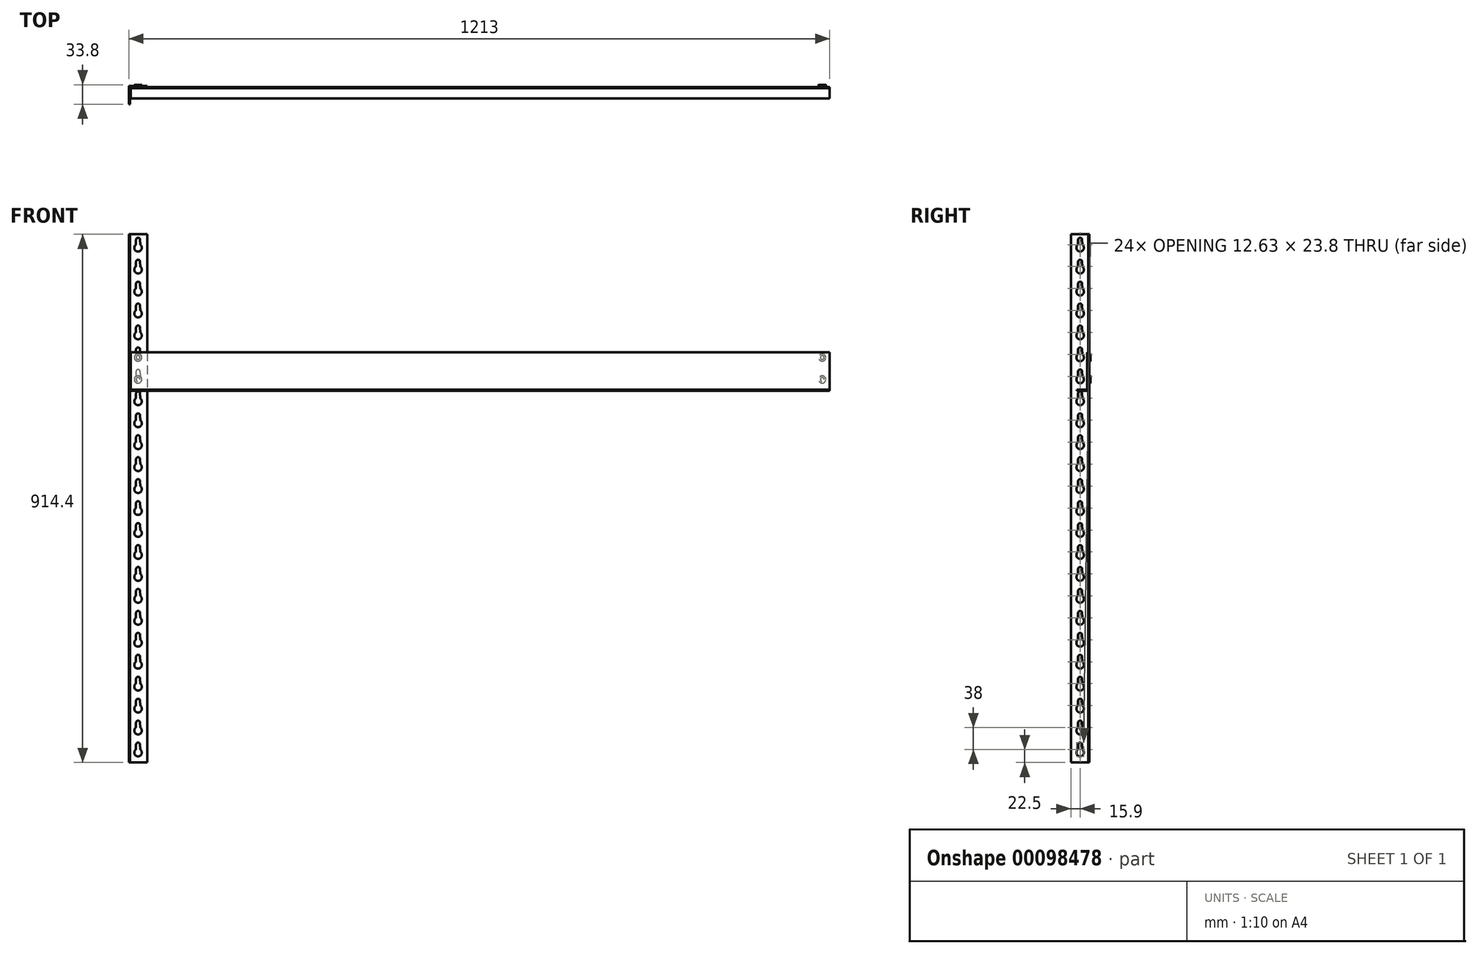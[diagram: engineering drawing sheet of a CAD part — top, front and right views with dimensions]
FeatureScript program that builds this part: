
annotation { "Feature Type Name" : "Feature", "Feature Type Description" : "" }
export const myFeature = defineFeature(function(context is Context, id is Id, definition is map)
    precondition{}
    {
        {
            var Q0;
            Q0=qCreatedBy(makeId("Top.planeOp"),FACE);
            var sketch = newSketch(context, id + "F0", { "sketchPlane" : qUnion([Q0])});
            skLineSegment(sketch, "E0.bottom", {"start": v(-13.9, -15.9) * mm, "end": v(-15.9, -15.9) * mm});
            skLineSegment(sketch, "E0.top", {"start": v(15.9, 15.9) * mm, "end": v(-14.9, 15.9) * mm});
            skLineSegment(sketch, "E0.left", {"start": v(15.9, 13.9) * mm, "end": v(15.9, 15.9) * mm});
            skLineSegment(sketch, "E0.right", {"start": v(-15.9, -15.9) * mm, "end": v(-15.9, 14.9) * mm});
            skPoint(sketch, "E0.middle", {"position": v(0, 0) * mm});
            skLineSegment(sketch, "E1.0", {"start": v(13.9, 13.9) * mm, "end": v(-12.9, 13.9) * mm});
            skLineSegment(sketch, "E1.3", {"start": v(-13.9, -13.9) * mm, "end": v(-13.9, 12.9) * mm});
            skLineSegment(sketch, "E2", {"start": v(13.9, 13.9) * mm, "end": v(15.9, 13.9) * mm});
            skLineSegment(sketch, "E3", {"start": v(-13.9, -13.9) * mm, "end": v(-13.9, -15.9) * mm});
            skPoint(sketch, "E4.orphan", {"position": v(15.9, -15.9) * mm});
            skPoint(sketch, "E5.visualSharp", {"position": v(-15.9, 15.9) * mm});
            skArc(sketch, "E5.filletArc", {"start": v(-14.9, 15.9) * mm, "mid": v(-15.6, 15.6) * mm, "end": v(-15.9, 14.9) * mm});
            skPoint(sketch, "E6.visualSharp", {"position": v(-13.9, 13.9) * mm});
            skArc(sketch, "E6.filletArc", {"start": v(-12.9, 13.9) * mm, "mid": v(-13.6, 13.6) * mm, "end": v(-13.9, 12.9) * mm});
            skSolve(sketch);
        }
        {
            var Q0;
            Q0 = qSketchRegion(id + "F0", true);
            extrude(context, id + "F1", {"entities" : qUnion([Q0]), "depth" : 914.4 * mm});
        }
        {
            var Q0;
            Q0=makeQuery(id+"F1.opExtrude","SWEPT_FACE",FACE,{"disambiguationData":[OSD([sQuery(id+"F0.wireOp",EDGE,"E0.right")])]});
            var sketch = newSketch(context, id + "F2", { "sketchPlane" : qUnion([Q0])});
            skArc(sketch, "E7", {"start": v(-4.32, 895.96) * mm, "mid": v(0, 884.6) * mm, "end": v(4.32, 895.96) * mm});
            skArc(sketch, "E8", {"start": v(3.5, 904.9) * mm, "mid": v(0, 908.4) * mm, "end": v(-3.5, 904.9) * mm});
            skLineSegment(sketch, "E9", {"start": v(0, 904.9) * mm, "end": v(-3.5, 904.9) * mm, "construction": true});
            skLineSegment(sketch, "E10", {"start": v(0, 891.1) * mm, "end": v(-6.5, 891.1) * mm, "construction": true});
            skLineSegment(sketch, "E11", {"start": v(0, 904.9) * mm, "end": v(0, 891.1) * mm, "construction": true});
            skLineSegment(sketch, "E12", {"start": v(-3.5, 904.9) * mm, "end": v(-3.65, 897.41) * mm});
            skLineSegment(sketch, "E13.MirrorCS", {"start": v(3.5, 904.9) * mm, "end": v(3.65, 897.41) * mm});
            skPoint(sketch, "E14.visualSharp", {"position": v(-3.67, 896.47) * mm});
            skArc(sketch, "E14.filletArc", {"start": v(-4.32, 895.96) * mm, "mid": v(-3.83, 896.61) * mm, "end": v(-3.65, 897.41) * mm});
            skPoint(sketch, "E15.visualSharp", {"position": v(3.67, 896.47) * mm});
            skArc(sketch, "E15.filletArc", {"start": v(3.65, 897.41) * mm, "mid": v(3.83, 896.61) * mm, "end": v(4.32, 895.96) * mm});
            skArc(sketch, "E16.0.1.0", {"start": v(3.5, 866.9) * mm, "mid": v(0, 870.4) * mm, "end": v(-3.5, 866.9) * mm});
            skLineSegment(sketch, "E16.0.1.1", {"start": v(-3.5, 866.9) * mm, "end": v(-3.65, 859.41) * mm});
            skLineSegment(sketch, "E16.0.1.2", {"start": v(3.5, 866.9) * mm, "end": v(3.65, 859.41) * mm});
            skArc(sketch, "E16.0.1.3", {"start": v(-4.32, 857.96) * mm, "mid": v(0, 846.6) * mm, "end": v(4.32, 857.96) * mm});
            skArc(sketch, "E16.0.1.4", {"start": v(-4.32, 857.96) * mm, "mid": v(-3.83, 858.61) * mm, "end": v(-3.65, 859.41) * mm});
            skArc(sketch, "E16.0.1.5", {"start": v(3.65, 859.41) * mm, "mid": v(3.83, 858.61) * mm, "end": v(4.32, 857.96) * mm});
            skArc(sketch, "E16.0.2.0", {"start": v(3.5, 828.9) * mm, "mid": v(0, 832.4) * mm, "end": v(-3.5, 828.9) * mm});
            skLineSegment(sketch, "E16.0.2.1", {"start": v(-3.5, 828.9) * mm, "end": v(-3.65, 821.41) * mm});
            skLineSegment(sketch, "E16.0.2.2", {"start": v(3.5, 828.9) * mm, "end": v(3.65, 821.41) * mm});
            skArc(sketch, "E16.0.2.3", {"start": v(-4.32, 819.96) * mm, "mid": v(0, 808.6) * mm, "end": v(4.32, 819.96) * mm});
            skArc(sketch, "E16.0.2.4", {"start": v(-4.32, 819.96) * mm, "mid": v(-3.83, 820.61) * mm, "end": v(-3.65, 821.41) * mm});
            skArc(sketch, "E16.0.2.5", {"start": v(3.65, 821.41) * mm, "mid": v(3.83, 820.61) * mm, "end": v(4.32, 819.96) * mm});
            skArc(sketch, "E16.0.3.0", {"start": v(3.5, 790.9) * mm, "mid": v(0, 794.4) * mm, "end": v(-3.5, 790.9) * mm});
            skLineSegment(sketch, "E16.0.3.1", {"start": v(-3.5, 790.9) * mm, "end": v(-3.65, 783.41) * mm});
            skLineSegment(sketch, "E16.0.3.2", {"start": v(3.5, 790.9) * mm, "end": v(3.65, 783.41) * mm});
            skArc(sketch, "E16.0.3.3", {"start": v(-4.32, 781.96) * mm, "mid": v(0, 770.6) * mm, "end": v(4.32, 781.96) * mm});
            skArc(sketch, "E16.0.3.4", {"start": v(-4.32, 781.96) * mm, "mid": v(-3.83, 782.61) * mm, "end": v(-3.65, 783.41) * mm});
            skArc(sketch, "E16.0.3.5", {"start": v(3.65, 783.41) * mm, "mid": v(3.83, 782.61) * mm, "end": v(4.32, 781.96) * mm});
            skArc(sketch, "E16.0.4.0", {"start": v(3.5, 752.9) * mm, "mid": v(0, 756.4) * mm, "end": v(-3.5, 752.9) * mm});
            skLineSegment(sketch, "E16.0.4.1", {"start": v(-3.5, 752.9) * mm, "end": v(-3.65, 745.41) * mm});
            skLineSegment(sketch, "E16.0.4.2", {"start": v(3.5, 752.9) * mm, "end": v(3.65, 745.41) * mm});
            skArc(sketch, "E16.0.4.3", {"start": v(-4.32, 743.96) * mm, "mid": v(0, 732.6) * mm, "end": v(4.32, 743.96) * mm});
            skArc(sketch, "E16.0.4.4", {"start": v(-4.32, 743.96) * mm, "mid": v(-3.83, 744.61) * mm, "end": v(-3.65, 745.41) * mm});
            skArc(sketch, "E16.0.4.5", {"start": v(3.65, 745.41) * mm, "mid": v(3.83, 744.61) * mm, "end": v(4.32, 743.96) * mm});
            skArc(sketch, "E16.0.5.0", {"start": v(3.5, 714.9) * mm, "mid": v(0, 718.4) * mm, "end": v(-3.5, 714.9) * mm});
            skLineSegment(sketch, "E16.0.5.1", {"start": v(-3.5, 714.9) * mm, "end": v(-3.65, 707.41) * mm});
            skLineSegment(sketch, "E16.0.5.2", {"start": v(3.5, 714.9) * mm, "end": v(3.65, 707.41) * mm});
            skArc(sketch, "E16.0.5.3", {"start": v(-4.32, 705.96) * mm, "mid": v(0, 694.6) * mm, "end": v(4.32, 705.96) * mm});
            skArc(sketch, "E16.0.5.4", {"start": v(-4.32, 705.96) * mm, "mid": v(-3.83, 706.61) * mm, "end": v(-3.65, 707.41) * mm});
            skArc(sketch, "E16.0.5.5", {"start": v(3.65, 707.41) * mm, "mid": v(3.83, 706.61) * mm, "end": v(4.32, 705.96) * mm});
            skArc(sketch, "E16.0.6.0", {"start": v(3.5, 676.9) * mm, "mid": v(0, 680.4) * mm, "end": v(-3.5, 676.9) * mm});
            skLineSegment(sketch, "E16.0.6.1", {"start": v(-3.5, 676.9) * mm, "end": v(-3.65, 669.41) * mm});
            skLineSegment(sketch, "E16.0.6.2", {"start": v(3.5, 676.9) * mm, "end": v(3.65, 669.41) * mm});
            skArc(sketch, "E16.0.6.3", {"start": v(-4.32, 667.96) * mm, "mid": v(0, 656.6) * mm, "end": v(4.32, 667.96) * mm});
            skArc(sketch, "E16.0.6.4", {"start": v(-4.32, 667.96) * mm, "mid": v(-3.83, 668.61) * mm, "end": v(-3.65, 669.41) * mm});
            skArc(sketch, "E16.0.6.5", {"start": v(3.65, 669.41) * mm, "mid": v(3.83, 668.61) * mm, "end": v(4.32, 667.96) * mm});
            skArc(sketch, "E16.0.7.0", {"start": v(3.5, 638.9) * mm, "mid": v(0, 642.4) * mm, "end": v(-3.5, 638.9) * mm});
            skLineSegment(sketch, "E16.0.7.1", {"start": v(-3.5, 638.9) * mm, "end": v(-3.65, 631.41) * mm});
            skLineSegment(sketch, "E16.0.7.2", {"start": v(3.5, 638.9) * mm, "end": v(3.65, 631.41) * mm});
            skArc(sketch, "E16.0.7.3", {"start": v(-4.32, 629.96) * mm, "mid": v(0, 618.6) * mm, "end": v(4.32, 629.96) * mm});
            skArc(sketch, "E16.0.7.4", {"start": v(-4.32, 629.96) * mm, "mid": v(-3.83, 630.61) * mm, "end": v(-3.65, 631.41) * mm});
            skArc(sketch, "E16.0.7.5", {"start": v(3.65, 631.41) * mm, "mid": v(3.83, 630.61) * mm, "end": v(4.32, 629.96) * mm});
            skArc(sketch, "E16.0.8.0", {"start": v(3.5, 600.9) * mm, "mid": v(0, 604.4) * mm, "end": v(-3.5, 600.9) * mm});
            skLineSegment(sketch, "E16.0.8.1", {"start": v(-3.5, 600.9) * mm, "end": v(-3.65, 593.41) * mm});
            skLineSegment(sketch, "E16.0.8.2", {"start": v(3.5, 600.9) * mm, "end": v(3.65, 593.41) * mm});
            skArc(sketch, "E16.0.8.3", {"start": v(-4.32, 591.96) * mm, "mid": v(0, 580.6) * mm, "end": v(4.32, 591.96) * mm});
            skArc(sketch, "E16.0.8.4", {"start": v(-4.32, 591.96) * mm, "mid": v(-3.83, 592.61) * mm, "end": v(-3.65, 593.41) * mm});
            skArc(sketch, "E16.0.8.5", {"start": v(3.65, 593.41) * mm, "mid": v(3.83, 592.61) * mm, "end": v(4.32, 591.96) * mm});
            skArc(sketch, "E16.0.9.0", {"start": v(3.5, 562.9) * mm, "mid": v(0, 566.4) * mm, "end": v(-3.5, 562.9) * mm});
            skLineSegment(sketch, "E16.0.9.1", {"start": v(-3.5, 562.9) * mm, "end": v(-3.65, 555.41) * mm});
            skLineSegment(sketch, "E16.0.9.2", {"start": v(3.5, 562.9) * mm, "end": v(3.65, 555.41) * mm});
            skArc(sketch, "E16.0.9.3", {"start": v(-4.32, 553.96) * mm, "mid": v(0, 542.6) * mm, "end": v(4.32, 553.96) * mm});
            skArc(sketch, "E16.0.9.4", {"start": v(-4.32, 553.96) * mm, "mid": v(-3.83, 554.61) * mm, "end": v(-3.65, 555.41) * mm});
            skArc(sketch, "E16.0.9.5", {"start": v(3.65, 555.41) * mm, "mid": v(3.83, 554.61) * mm, "end": v(4.32, 553.96) * mm});
            skArc(sketch, "E16.0.10.0", {"start": v(3.5, 524.9) * mm, "mid": v(0, 528.4) * mm, "end": v(-3.5, 524.9) * mm});
            skLineSegment(sketch, "E16.0.10.1", {"start": v(-3.5, 524.9) * mm, "end": v(-3.65, 517.41) * mm});
            skLineSegment(sketch, "E16.0.10.2", {"start": v(3.5, 524.9) * mm, "end": v(3.65, 517.41) * mm});
            skArc(sketch, "E16.0.10.3", {"start": v(-4.32, 515.96) * mm, "mid": v(0, 504.6) * mm, "end": v(4.32, 515.96) * mm});
            skArc(sketch, "E16.0.10.4", {"start": v(-4.32, 515.96) * mm, "mid": v(-3.83, 516.61) * mm, "end": v(-3.65, 517.41) * mm});
            skArc(sketch, "E16.0.10.5", {"start": v(3.65, 517.41) * mm, "mid": v(3.83, 516.61) * mm, "end": v(4.32, 515.96) * mm});
            skArc(sketch, "E16.0.11.0", {"start": v(3.5, 486.9) * mm, "mid": v(0, 490.4) * mm, "end": v(-3.5, 486.9) * mm});
            skLineSegment(sketch, "E16.0.11.1", {"start": v(-3.5, 486.9) * mm, "end": v(-3.65, 479.41) * mm});
            skLineSegment(sketch, "E16.0.11.2", {"start": v(3.5, 486.9) * mm, "end": v(3.65, 479.41) * mm});
            skArc(sketch, "E16.0.11.3", {"start": v(-4.32, 477.96) * mm, "mid": v(0, 466.6) * mm, "end": v(4.32, 477.96) * mm});
            skArc(sketch, "E16.0.11.4", {"start": v(-4.32, 477.96) * mm, "mid": v(-3.83, 478.61) * mm, "end": v(-3.65, 479.41) * mm});
            skArc(sketch, "E16.0.11.5", {"start": v(3.65, 479.41) * mm, "mid": v(3.83, 478.61) * mm, "end": v(4.32, 477.96) * mm});
            skArc(sketch, "E16.0.12.0", {"start": v(3.5, 448.9) * mm, "mid": v(0, 452.4) * mm, "end": v(-3.5, 448.9) * mm});
            skLineSegment(sketch, "E16.0.12.1", {"start": v(-3.5, 448.9) * mm, "end": v(-3.65, 441.41) * mm});
            skLineSegment(sketch, "E16.0.12.2", {"start": v(3.5, 448.9) * mm, "end": v(3.65, 441.41) * mm});
            skArc(sketch, "E16.0.12.3", {"start": v(-4.32, 439.96) * mm, "mid": v(0, 428.6) * mm, "end": v(4.32, 439.96) * mm});
            skArc(sketch, "E16.0.12.4", {"start": v(-4.32, 439.96) * mm, "mid": v(-3.83, 440.61) * mm, "end": v(-3.65, 441.41) * mm});
            skArc(sketch, "E16.0.12.5", {"start": v(3.65, 441.41) * mm, "mid": v(3.83, 440.61) * mm, "end": v(4.32, 439.96) * mm});
            skArc(sketch, "E16.0.13.0", {"start": v(3.5, 410.9) * mm, "mid": v(0, 414.4) * mm, "end": v(-3.5, 410.9) * mm});
            skLineSegment(sketch, "E16.0.13.1", {"start": v(-3.5, 410.9) * mm, "end": v(-3.65, 403.41) * mm});
            skLineSegment(sketch, "E16.0.13.2", {"start": v(3.5, 410.9) * mm, "end": v(3.65, 403.41) * mm});
            skArc(sketch, "E16.0.13.3", {"start": v(-4.32, 401.96) * mm, "mid": v(0, 390.6) * mm, "end": v(4.32, 401.96) * mm});
            skArc(sketch, "E16.0.13.4", {"start": v(-4.32, 401.96) * mm, "mid": v(-3.83, 402.61) * mm, "end": v(-3.65, 403.41) * mm});
            skArc(sketch, "E16.0.13.5", {"start": v(3.65, 403.41) * mm, "mid": v(3.83, 402.61) * mm, "end": v(4.32, 401.96) * mm});
            skArc(sketch, "E16.0.14.0", {"start": v(3.5, 372.9) * mm, "mid": v(0, 376.4) * mm, "end": v(-3.5, 372.9) * mm});
            skLineSegment(sketch, "E16.0.14.1", {"start": v(-3.5, 372.9) * mm, "end": v(-3.65, 365.41) * mm});
            skLineSegment(sketch, "E16.0.14.2", {"start": v(3.5, 372.9) * mm, "end": v(3.65, 365.41) * mm});
            skArc(sketch, "E16.0.14.3", {"start": v(-4.32, 363.96) * mm, "mid": v(0, 352.6) * mm, "end": v(4.32, 363.96) * mm});
            skArc(sketch, "E16.0.14.4", {"start": v(-4.32, 363.96) * mm, "mid": v(-3.83, 364.61) * mm, "end": v(-3.65, 365.41) * mm});
            skArc(sketch, "E16.0.14.5", {"start": v(3.65, 365.41) * mm, "mid": v(3.83, 364.61) * mm, "end": v(4.32, 363.96) * mm});
            skArc(sketch, "E16.0.15.0", {"start": v(3.5, 334.9) * mm, "mid": v(0, 338.4) * mm, "end": v(-3.5, 334.9) * mm});
            skLineSegment(sketch, "E16.0.15.1", {"start": v(-3.5, 334.9) * mm, "end": v(-3.65, 327.41) * mm});
            skLineSegment(sketch, "E16.0.15.2", {"start": v(3.5, 334.9) * mm, "end": v(3.65, 327.41) * mm});
            skArc(sketch, "E16.0.15.3", {"start": v(-4.32, 325.96) * mm, "mid": v(0, 314.6) * mm, "end": v(4.32, 325.96) * mm});
            skArc(sketch, "E16.0.15.4", {"start": v(-4.32, 325.96) * mm, "mid": v(-3.83, 326.61) * mm, "end": v(-3.65, 327.41) * mm});
            skArc(sketch, "E16.0.15.5", {"start": v(3.65, 327.41) * mm, "mid": v(3.83, 326.61) * mm, "end": v(4.32, 325.96) * mm});
            skArc(sketch, "E16.0.16.0", {"start": v(3.5, 296.9) * mm, "mid": v(0, 300.4) * mm, "end": v(-3.5, 296.9) * mm});
            skLineSegment(sketch, "E16.0.16.1", {"start": v(-3.5, 296.9) * mm, "end": v(-3.65, 289.41) * mm});
            skLineSegment(sketch, "E16.0.16.2", {"start": v(3.5, 296.9) * mm, "end": v(3.65, 289.41) * mm});
            skArc(sketch, "E16.0.16.3", {"start": v(-4.32, 287.96) * mm, "mid": v(0, 276.6) * mm, "end": v(4.32, 287.96) * mm});
            skArc(sketch, "E16.0.16.4", {"start": v(-4.32, 287.96) * mm, "mid": v(-3.83, 288.61) * mm, "end": v(-3.65, 289.41) * mm});
            skArc(sketch, "E16.0.16.5", {"start": v(3.65, 289.41) * mm, "mid": v(3.83, 288.61) * mm, "end": v(4.32, 287.96) * mm});
            skArc(sketch, "E16.0.17.0", {"start": v(3.5, 258.9) * mm, "mid": v(0, 262.4) * mm, "end": v(-3.5, 258.9) * mm});
            skLineSegment(sketch, "E16.0.17.1", {"start": v(-3.5, 258.9) * mm, "end": v(-3.65, 251.41) * mm});
            skLineSegment(sketch, "E16.0.17.2", {"start": v(3.5, 258.9) * mm, "end": v(3.65, 251.41) * mm});
            skArc(sketch, "E16.0.17.3", {"start": v(-4.32, 249.96) * mm, "mid": v(0, 238.6) * mm, "end": v(4.32, 249.96) * mm});
            skArc(sketch, "E16.0.17.4", {"start": v(-4.32, 249.96) * mm, "mid": v(-3.83, 250.61) * mm, "end": v(-3.65, 251.41) * mm});
            skArc(sketch, "E16.0.17.5", {"start": v(3.65, 251.41) * mm, "mid": v(3.83, 250.61) * mm, "end": v(4.32, 249.96) * mm});
            skArc(sketch, "E16.0.18.0", {"start": v(3.5, 220.9) * mm, "mid": v(0, 224.4) * mm, "end": v(-3.5, 220.9) * mm});
            skLineSegment(sketch, "E16.0.18.1", {"start": v(-3.5, 220.9) * mm, "end": v(-3.65, 213.41) * mm});
            skLineSegment(sketch, "E16.0.18.2", {"start": v(3.5, 220.9) * mm, "end": v(3.65, 213.41) * mm});
            skArc(sketch, "E16.0.18.3", {"start": v(-4.32, 211.96) * mm, "mid": v(0, 200.6) * mm, "end": v(4.32, 211.96) * mm});
            skArc(sketch, "E16.0.18.4", {"start": v(-4.32, 211.96) * mm, "mid": v(-3.83, 212.61) * mm, "end": v(-3.65, 213.41) * mm});
            skArc(sketch, "E16.0.18.5", {"start": v(3.65, 213.41) * mm, "mid": v(3.83, 212.61) * mm, "end": v(4.32, 211.96) * mm});
            skArc(sketch, "E16.0.19.0", {"start": v(3.5, 182.9) * mm, "mid": v(0, 186.4) * mm, "end": v(-3.5, 182.9) * mm});
            skLineSegment(sketch, "E16.0.19.1", {"start": v(-3.5, 182.9) * mm, "end": v(-3.65, 175.41) * mm});
            skLineSegment(sketch, "E16.0.19.2", {"start": v(3.5, 182.9) * mm, "end": v(3.65, 175.41) * mm});
            skArc(sketch, "E16.0.19.3", {"start": v(-4.32, 173.96) * mm, "mid": v(0, 162.6) * mm, "end": v(4.32, 173.96) * mm});
            skArc(sketch, "E16.0.19.4", {"start": v(-4.32, 173.96) * mm, "mid": v(-3.83, 174.61) * mm, "end": v(-3.65, 175.41) * mm});
            skArc(sketch, "E16.0.19.5", {"start": v(3.65, 175.41) * mm, "mid": v(3.83, 174.61) * mm, "end": v(4.32, 173.96) * mm});
            skArc(sketch, "E16.0.20.0", {"start": v(3.5, 144.9) * mm, "mid": v(0, 148.4) * mm, "end": v(-3.5, 144.9) * mm});
            skLineSegment(sketch, "E16.0.20.1", {"start": v(-3.5, 144.9) * mm, "end": v(-3.65, 137.41) * mm});
            skLineSegment(sketch, "E16.0.20.2", {"start": v(3.5, 144.9) * mm, "end": v(3.65, 137.41) * mm});
            skArc(sketch, "E16.0.20.3", {"start": v(-4.32, 135.96) * mm, "mid": v(0, 124.6) * mm, "end": v(4.32, 135.96) * mm});
            skArc(sketch, "E16.0.20.4", {"start": v(-4.32, 135.96) * mm, "mid": v(-3.83, 136.61) * mm, "end": v(-3.65, 137.41) * mm});
            skArc(sketch, "E16.0.20.5", {"start": v(3.65, 137.41) * mm, "mid": v(3.83, 136.61) * mm, "end": v(4.32, 135.96) * mm});
            skArc(sketch, "E16.0.21.0", {"start": v(3.5, 106.9) * mm, "mid": v(0, 110.4) * mm, "end": v(-3.5, 106.9) * mm});
            skLineSegment(sketch, "E16.0.21.1", {"start": v(-3.5, 106.9) * mm, "end": v(-3.65, 99.41) * mm});
            skLineSegment(sketch, "E16.0.21.2", {"start": v(3.5, 106.9) * mm, "end": v(3.65, 99.41) * mm});
            skArc(sketch, "E16.0.21.3", {"start": v(-4.32, 97.96) * mm, "mid": v(0, 86.6) * mm, "end": v(4.32, 97.96) * mm});
            skArc(sketch, "E16.0.21.4", {"start": v(-4.32, 97.96) * mm, "mid": v(-3.83, 98.61) * mm, "end": v(-3.65, 99.41) * mm});
            skArc(sketch, "E16.0.21.5", {"start": v(3.65, 99.41) * mm, "mid": v(3.83, 98.61) * mm, "end": v(4.32, 97.96) * mm});
            skArc(sketch, "E16.0.22.0", {"start": v(3.5, 68.9) * mm, "mid": v(0, 72.4) * mm, "end": v(-3.5, 68.9) * mm});
            skLineSegment(sketch, "E16.0.22.1", {"start": v(-3.5, 68.9) * mm, "end": v(-3.65, 61.41) * mm});
            skLineSegment(sketch, "E16.0.22.2", {"start": v(3.5, 68.9) * mm, "end": v(3.65, 61.41) * mm});
            skArc(sketch, "E16.0.22.3", {"start": v(-4.32, 59.96) * mm, "mid": v(0, 48.6) * mm, "end": v(4.32, 59.96) * mm});
            skArc(sketch, "E16.0.22.4", {"start": v(-4.32, 59.96) * mm, "mid": v(-3.83, 60.61) * mm, "end": v(-3.65, 61.41) * mm});
            skArc(sketch, "E16.0.22.5", {"start": v(3.65, 61.41) * mm, "mid": v(3.83, 60.61) * mm, "end": v(4.32, 59.96) * mm});
            skLineSegment(sketch, "E16.direction1", {"start": v(-3.5, 904.9) * mm, "end": v(21.5, 904.9) * mm, "construction": true});
            skLineSegment(sketch, "E16.direction2", {"start": v(-3.5, 904.9) * mm, "end": v(-3.5, 866.9) * mm, "construction": true});
            skArc(sketch, "E17.0.0.23", {"start": v(3.5, 30.9) * mm, "mid": v(0, 34.4) * mm, "end": v(-3.5, 30.9) * mm});
            skLineSegment(sketch, "E17.4.0.23", {"start": v(-3.5, 30.9) * mm, "end": v(-3.65, 23.41) * mm});
            skLineSegment(sketch, "E17.7.0.23", {"start": v(3.5, 30.9) * mm, "end": v(3.65, 23.41) * mm});
            skArc(sketch, "E17.10.0.23", {"start": v(-4.32, 21.96) * mm, "mid": v(0, 10.6) * mm, "end": v(4.32, 21.96) * mm});
            skArc(sketch, "E17.14.0.23", {"start": v(-4.32, 21.96) * mm, "mid": v(-3.83, 22.61) * mm, "end": v(-3.65, 23.41) * mm});
            skArc(sketch, "E17.18.0.23", {"start": v(3.65, 23.41) * mm, "mid": v(3.83, 22.61) * mm, "end": v(4.32, 21.96) * mm});
            skSolve(sketch);
        }
        {
            var Q0;
            Q0 = qSketchRegion(id + "F2", true);
            extrude(context, id + "F3", {"entities" : qUnion([Q0]), "operationType" : NewBodyOperationType.REMOVE, "endBound" : BoundingType.UP_TO_NEXT, "oppositeDirection" : true, "depth" : 25 * mm});
        }
        {
            var Q0;
            Q0=makeQuery(id+"F1.opExtrude","SWEPT_FACE",FACE,{"disambiguationData":[OSD([sQuery(id+"F0.wireOp",EDGE,"E0.top")])]});
            var sketch = newSketch(context, id + "F4", { "sketchPlane" : qUnion([Q0])});
            skArc(sketch, "E18", {"start": v(3.5, 904.9) * mm, "mid": v(0, 908.4) * mm, "end": v(-3.5, 904.9) * mm});
            skArc(sketch, "E19", {"start": v(-4.61, 895.68) * mm, "mid": v(0, 884.6) * mm, "end": v(4.61, 895.68) * mm});
            skLineSegment(sketch, "E20", {"start": v(0, 904.9) * mm, "end": v(-3.5, 904.9) * mm, "construction": true});
            skLineSegment(sketch, "E21", {"start": v(0, 891.1) * mm, "end": v(-6.5, 891.1) * mm, "construction": true});
            skLineSegment(sketch, "E22", {"start": v(-3.5, 904.9) * mm, "end": v(-4.03, 896.96) * mm});
            skLineSegment(sketch, "E23", {"start": v(0, 904.9) * mm, "end": v(0, 889.93) * mm, "construction": true});
            skLineSegment(sketch, "E24.MirrorCS", {"start": v(3.5, 904.9) * mm, "end": v(4.03, 896.96) * mm});
            skPoint(sketch, "E25.visualSharp", {"position": v(-4.09, 896.15) * mm});
            skArc(sketch, "E25.filletArc", {"start": v(-4.61, 895.68) * mm, "mid": v(-4.2, 896.27) * mm, "end": v(-4.03, 896.96) * mm});
            skPoint(sketch, "E26.visualSharp", {"position": v(4.09, 896.15) * mm});
            skArc(sketch, "E26.filletArc", {"start": v(4.03, 896.96) * mm, "mid": v(4.2, 896.27) * mm, "end": v(4.61, 895.68) * mm});
            skArc(sketch, "E27.0.1.0", {"start": v(3.5, 866.9) * mm, "mid": v(0, 870.4) * mm, "end": v(-3.5, 866.9) * mm});
            skLineSegment(sketch, "E27.0.1.1", {"start": v(-3.5, 866.9) * mm, "end": v(-4.03, 858.96) * mm});
            skLineSegment(sketch, "E27.0.1.2", {"start": v(3.5, 866.9) * mm, "end": v(4.03, 858.96) * mm});
            skArc(sketch, "E27.0.1.3", {"start": v(-4.61, 857.68) * mm, "mid": v(0, 846.6) * mm, "end": v(4.61, 857.68) * mm});
            skArc(sketch, "E27.0.1.4", {"start": v(-4.61, 857.68) * mm, "mid": v(-4.2, 858.27) * mm, "end": v(-4.03, 858.96) * mm});
            skArc(sketch, "E27.0.1.5", {"start": v(4.03, 858.96) * mm, "mid": v(4.2, 858.27) * mm, "end": v(4.61, 857.68) * mm});
            skArc(sketch, "E27.0.2.0", {"start": v(3.5, 828.9) * mm, "mid": v(0, 832.4) * mm, "end": v(-3.5, 828.9) * mm});
            skLineSegment(sketch, "E27.0.2.1", {"start": v(-3.5, 828.9) * mm, "end": v(-4.03, 820.96) * mm});
            skLineSegment(sketch, "E27.0.2.2", {"start": v(3.5, 828.9) * mm, "end": v(4.03, 820.96) * mm});
            skArc(sketch, "E27.0.2.3", {"start": v(-4.61, 819.68) * mm, "mid": v(0, 808.6) * mm, "end": v(4.61, 819.68) * mm});
            skArc(sketch, "E27.0.2.4", {"start": v(-4.61, 819.68) * mm, "mid": v(-4.2, 820.27) * mm, "end": v(-4.03, 820.96) * mm});
            skArc(sketch, "E27.0.2.5", {"start": v(4.03, 820.96) * mm, "mid": v(4.2, 820.27) * mm, "end": v(4.61, 819.68) * mm});
            skArc(sketch, "E27.0.3.0", {"start": v(3.5, 790.9) * mm, "mid": v(0, 794.4) * mm, "end": v(-3.5, 790.9) * mm});
            skLineSegment(sketch, "E27.0.3.1", {"start": v(-3.5, 790.9) * mm, "end": v(-4.03, 782.96) * mm});
            skLineSegment(sketch, "E27.0.3.2", {"start": v(3.5, 790.9) * mm, "end": v(4.03, 782.96) * mm});
            skArc(sketch, "E27.0.3.3", {"start": v(-4.61, 781.68) * mm, "mid": v(0, 770.6) * mm, "end": v(4.61, 781.68) * mm});
            skArc(sketch, "E27.0.3.4", {"start": v(-4.61, 781.68) * mm, "mid": v(-4.2, 782.27) * mm, "end": v(-4.03, 782.96) * mm});
            skArc(sketch, "E27.0.3.5", {"start": v(4.03, 782.96) * mm, "mid": v(4.2, 782.27) * mm, "end": v(4.61, 781.68) * mm});
            skArc(sketch, "E27.0.4.0", {"start": v(3.5, 752.9) * mm, "mid": v(0, 756.4) * mm, "end": v(-3.5, 752.9) * mm});
            skLineSegment(sketch, "E27.0.4.1", {"start": v(-3.5, 752.9) * mm, "end": v(-4.03, 744.96) * mm});
            skLineSegment(sketch, "E27.0.4.2", {"start": v(3.5, 752.9) * mm, "end": v(4.03, 744.96) * mm});
            skArc(sketch, "E27.0.4.3", {"start": v(-4.61, 743.68) * mm, "mid": v(0, 732.6) * mm, "end": v(4.61, 743.68) * mm});
            skArc(sketch, "E27.0.4.4", {"start": v(-4.61, 743.68) * mm, "mid": v(-4.2, 744.27) * mm, "end": v(-4.03, 744.96) * mm});
            skArc(sketch, "E27.0.4.5", {"start": v(4.03, 744.96) * mm, "mid": v(4.2, 744.27) * mm, "end": v(4.61, 743.68) * mm});
            skArc(sketch, "E27.0.5.0", {"start": v(3.5, 714.9) * mm, "mid": v(0, 718.4) * mm, "end": v(-3.5, 714.9) * mm});
            skLineSegment(sketch, "E27.0.5.1", {"start": v(-3.5, 714.9) * mm, "end": v(-4.03, 706.96) * mm});
            skLineSegment(sketch, "E27.0.5.2", {"start": v(3.5, 714.9) * mm, "end": v(4.03, 706.96) * mm});
            skArc(sketch, "E27.0.5.3", {"start": v(-4.61, 705.68) * mm, "mid": v(0, 694.6) * mm, "end": v(4.61, 705.68) * mm});
            skArc(sketch, "E27.0.5.4", {"start": v(-4.61, 705.68) * mm, "mid": v(-4.2, 706.27) * mm, "end": v(-4.03, 706.96) * mm});
            skArc(sketch, "E27.0.5.5", {"start": v(4.03, 706.96) * mm, "mid": v(4.2, 706.27) * mm, "end": v(4.61, 705.68) * mm});
            skArc(sketch, "E27.0.6.0", {"start": v(3.5, 676.9) * mm, "mid": v(0, 680.4) * mm, "end": v(-3.5, 676.9) * mm});
            skLineSegment(sketch, "E27.0.6.1", {"start": v(-3.5, 676.9) * mm, "end": v(-4.03, 668.96) * mm});
            skLineSegment(sketch, "E27.0.6.2", {"start": v(3.5, 676.9) * mm, "end": v(4.03, 668.96) * mm});
            skArc(sketch, "E27.0.6.3", {"start": v(-4.61, 667.68) * mm, "mid": v(0, 656.6) * mm, "end": v(4.61, 667.68) * mm});
            skArc(sketch, "E27.0.6.4", {"start": v(-4.61, 667.68) * mm, "mid": v(-4.2, 668.27) * mm, "end": v(-4.03, 668.96) * mm});
            skArc(sketch, "E27.0.6.5", {"start": v(4.03, 668.96) * mm, "mid": v(4.2, 668.27) * mm, "end": v(4.61, 667.68) * mm});
            skArc(sketch, "E27.0.7.0", {"start": v(3.5, 638.9) * mm, "mid": v(0, 642.4) * mm, "end": v(-3.5, 638.9) * mm});
            skLineSegment(sketch, "E27.0.7.1", {"start": v(-3.5, 638.9) * mm, "end": v(-4.03, 630.96) * mm});
            skLineSegment(sketch, "E27.0.7.2", {"start": v(3.5, 638.9) * mm, "end": v(4.03, 630.96) * mm});
            skArc(sketch, "E27.0.7.3", {"start": v(-4.61, 629.68) * mm, "mid": v(0, 618.6) * mm, "end": v(4.61, 629.68) * mm});
            skArc(sketch, "E27.0.7.4", {"start": v(-4.61, 629.68) * mm, "mid": v(-4.2, 630.27) * mm, "end": v(-4.03, 630.96) * mm});
            skArc(sketch, "E27.0.7.5", {"start": v(4.03, 630.96) * mm, "mid": v(4.2, 630.27) * mm, "end": v(4.61, 629.68) * mm});
            skArc(sketch, "E27.0.8.0", {"start": v(3.5, 600.9) * mm, "mid": v(0, 604.4) * mm, "end": v(-3.5, 600.9) * mm});
            skLineSegment(sketch, "E27.0.8.1", {"start": v(-3.5, 600.9) * mm, "end": v(-4.03, 592.96) * mm});
            skLineSegment(sketch, "E27.0.8.2", {"start": v(3.5, 600.9) * mm, "end": v(4.03, 592.96) * mm});
            skArc(sketch, "E27.0.8.3", {"start": v(-4.61, 591.68) * mm, "mid": v(0, 580.6) * mm, "end": v(4.61, 591.68) * mm});
            skArc(sketch, "E27.0.8.4", {"start": v(-4.61, 591.68) * mm, "mid": v(-4.2, 592.27) * mm, "end": v(-4.03, 592.96) * mm});
            skArc(sketch, "E27.0.8.5", {"start": v(4.03, 592.96) * mm, "mid": v(4.2, 592.27) * mm, "end": v(4.61, 591.68) * mm});
            skArc(sketch, "E27.0.9.0", {"start": v(3.5, 562.9) * mm, "mid": v(0, 566.4) * mm, "end": v(-3.5, 562.9) * mm});
            skLineSegment(sketch, "E27.0.9.1", {"start": v(-3.5, 562.9) * mm, "end": v(-4.03, 554.96) * mm});
            skLineSegment(sketch, "E27.0.9.2", {"start": v(3.5, 562.9) * mm, "end": v(4.03, 554.96) * mm});
            skArc(sketch, "E27.0.9.3", {"start": v(-4.61, 553.68) * mm, "mid": v(0, 542.6) * mm, "end": v(4.61, 553.68) * mm});
            skArc(sketch, "E27.0.9.4", {"start": v(-4.61, 553.68) * mm, "mid": v(-4.2, 554.27) * mm, "end": v(-4.03, 554.96) * mm});
            skArc(sketch, "E27.0.9.5", {"start": v(4.03, 554.96) * mm, "mid": v(4.2, 554.27) * mm, "end": v(4.61, 553.68) * mm});
            skArc(sketch, "E27.0.10.0", {"start": v(3.5, 524.9) * mm, "mid": v(0, 528.4) * mm, "end": v(-3.5, 524.9) * mm});
            skLineSegment(sketch, "E27.0.10.1", {"start": v(-3.5, 524.9) * mm, "end": v(-4.03, 516.96) * mm});
            skLineSegment(sketch, "E27.0.10.2", {"start": v(3.5, 524.9) * mm, "end": v(4.03, 516.96) * mm});
            skArc(sketch, "E27.0.10.3", {"start": v(-4.61, 515.68) * mm, "mid": v(0, 504.6) * mm, "end": v(4.61, 515.68) * mm});
            skArc(sketch, "E27.0.10.4", {"start": v(-4.61, 515.68) * mm, "mid": v(-4.2, 516.27) * mm, "end": v(-4.03, 516.96) * mm});
            skArc(sketch, "E27.0.10.5", {"start": v(4.03, 516.96) * mm, "mid": v(4.2, 516.27) * mm, "end": v(4.61, 515.68) * mm});
            skArc(sketch, "E27.0.11.0", {"start": v(3.5, 486.9) * mm, "mid": v(0, 490.4) * mm, "end": v(-3.5, 486.9) * mm});
            skLineSegment(sketch, "E27.0.11.1", {"start": v(-3.5, 486.9) * mm, "end": v(-4.03, 478.96) * mm});
            skLineSegment(sketch, "E27.0.11.2", {"start": v(3.5, 486.9) * mm, "end": v(4.03, 478.96) * mm});
            skArc(sketch, "E27.0.11.3", {"start": v(-4.61, 477.68) * mm, "mid": v(0, 466.6) * mm, "end": v(4.61, 477.68) * mm});
            skArc(sketch, "E27.0.11.4", {"start": v(-4.61, 477.68) * mm, "mid": v(-4.2, 478.27) * mm, "end": v(-4.03, 478.96) * mm});
            skArc(sketch, "E27.0.11.5", {"start": v(4.03, 478.96) * mm, "mid": v(4.2, 478.27) * mm, "end": v(4.61, 477.68) * mm});
            skArc(sketch, "E27.0.12.0", {"start": v(3.5, 448.9) * mm, "mid": v(0, 452.4) * mm, "end": v(-3.5, 448.9) * mm});
            skLineSegment(sketch, "E27.0.12.1", {"start": v(-3.5, 448.9) * mm, "end": v(-4.03, 440.96) * mm});
            skLineSegment(sketch, "E27.0.12.2", {"start": v(3.5, 448.9) * mm, "end": v(4.03, 440.96) * mm});
            skArc(sketch, "E27.0.12.3", {"start": v(-4.61, 439.68) * mm, "mid": v(0, 428.6) * mm, "end": v(4.61, 439.68) * mm});
            skArc(sketch, "E27.0.12.4", {"start": v(-4.61, 439.68) * mm, "mid": v(-4.2, 440.27) * mm, "end": v(-4.03, 440.96) * mm});
            skArc(sketch, "E27.0.12.5", {"start": v(4.03, 440.96) * mm, "mid": v(4.2, 440.27) * mm, "end": v(4.61, 439.68) * mm});
            skArc(sketch, "E27.0.13.0", {"start": v(3.5, 410.9) * mm, "mid": v(0, 414.4) * mm, "end": v(-3.5, 410.9) * mm});
            skLineSegment(sketch, "E27.0.13.1", {"start": v(-3.5, 410.9) * mm, "end": v(-4.03, 402.96) * mm});
            skLineSegment(sketch, "E27.0.13.2", {"start": v(3.5, 410.9) * mm, "end": v(4.03, 402.96) * mm});
            skArc(sketch, "E27.0.13.3", {"start": v(-4.61, 401.68) * mm, "mid": v(0, 390.6) * mm, "end": v(4.61, 401.68) * mm});
            skArc(sketch, "E27.0.13.4", {"start": v(-4.61, 401.68) * mm, "mid": v(-4.2, 402.27) * mm, "end": v(-4.03, 402.96) * mm});
            skArc(sketch, "E27.0.13.5", {"start": v(4.03, 402.96) * mm, "mid": v(4.2, 402.27) * mm, "end": v(4.61, 401.68) * mm});
            skArc(sketch, "E27.0.14.0", {"start": v(3.5, 372.9) * mm, "mid": v(0, 376.4) * mm, "end": v(-3.5, 372.9) * mm});
            skLineSegment(sketch, "E27.0.14.1", {"start": v(-3.5, 372.9) * mm, "end": v(-4.03, 364.96) * mm});
            skLineSegment(sketch, "E27.0.14.2", {"start": v(3.5, 372.9) * mm, "end": v(4.03, 364.96) * mm});
            skArc(sketch, "E27.0.14.3", {"start": v(-4.61, 363.68) * mm, "mid": v(0, 352.6) * mm, "end": v(4.61, 363.68) * mm});
            skArc(sketch, "E27.0.14.4", {"start": v(-4.61, 363.68) * mm, "mid": v(-4.2, 364.27) * mm, "end": v(-4.03, 364.96) * mm});
            skArc(sketch, "E27.0.14.5", {"start": v(4.03, 364.96) * mm, "mid": v(4.2, 364.27) * mm, "end": v(4.61, 363.68) * mm});
            skArc(sketch, "E27.0.15.0", {"start": v(3.5, 334.9) * mm, "mid": v(0, 338.4) * mm, "end": v(-3.5, 334.9) * mm});
            skLineSegment(sketch, "E27.0.15.1", {"start": v(-3.5, 334.9) * mm, "end": v(-4.03, 326.96) * mm});
            skLineSegment(sketch, "E27.0.15.2", {"start": v(3.5, 334.9) * mm, "end": v(4.03, 326.96) * mm});
            skArc(sketch, "E27.0.15.3", {"start": v(-4.61, 325.68) * mm, "mid": v(0, 314.6) * mm, "end": v(4.61, 325.68) * mm});
            skArc(sketch, "E27.0.15.4", {"start": v(-4.61, 325.68) * mm, "mid": v(-4.2, 326.27) * mm, "end": v(-4.03, 326.96) * mm});
            skArc(sketch, "E27.0.15.5", {"start": v(4.03, 326.96) * mm, "mid": v(4.2, 326.27) * mm, "end": v(4.61, 325.68) * mm});
            skArc(sketch, "E27.0.16.0", {"start": v(3.5, 296.9) * mm, "mid": v(0, 300.4) * mm, "end": v(-3.5, 296.9) * mm});
            skLineSegment(sketch, "E27.0.16.1", {"start": v(-3.5, 296.9) * mm, "end": v(-4.03, 288.96) * mm});
            skLineSegment(sketch, "E27.0.16.2", {"start": v(3.5, 296.9) * mm, "end": v(4.03, 288.96) * mm});
            skArc(sketch, "E27.0.16.3", {"start": v(-4.61, 287.68) * mm, "mid": v(0, 276.6) * mm, "end": v(4.61, 287.68) * mm});
            skArc(sketch, "E27.0.16.4", {"start": v(-4.61, 287.68) * mm, "mid": v(-4.2, 288.27) * mm, "end": v(-4.03, 288.96) * mm});
            skArc(sketch, "E27.0.16.5", {"start": v(4.03, 288.96) * mm, "mid": v(4.2, 288.27) * mm, "end": v(4.61, 287.68) * mm});
            skArc(sketch, "E27.0.17.0", {"start": v(3.5, 258.9) * mm, "mid": v(0, 262.4) * mm, "end": v(-3.5, 258.9) * mm});
            skLineSegment(sketch, "E27.0.17.1", {"start": v(-3.5, 258.9) * mm, "end": v(-4.03, 250.96) * mm});
            skLineSegment(sketch, "E27.0.17.2", {"start": v(3.5, 258.9) * mm, "end": v(4.03, 250.96) * mm});
            skArc(sketch, "E27.0.17.3", {"start": v(-4.61, 249.68) * mm, "mid": v(0, 238.6) * mm, "end": v(4.61, 249.68) * mm});
            skArc(sketch, "E27.0.17.4", {"start": v(-4.61, 249.68) * mm, "mid": v(-4.2, 250.27) * mm, "end": v(-4.03, 250.96) * mm});
            skArc(sketch, "E27.0.17.5", {"start": v(4.03, 250.96) * mm, "mid": v(4.2, 250.27) * mm, "end": v(4.61, 249.68) * mm});
            skArc(sketch, "E27.0.18.0", {"start": v(3.5, 220.9) * mm, "mid": v(0, 224.4) * mm, "end": v(-3.5, 220.9) * mm});
            skLineSegment(sketch, "E27.0.18.1", {"start": v(-3.5, 220.9) * mm, "end": v(-4.03, 212.96) * mm});
            skLineSegment(sketch, "E27.0.18.2", {"start": v(3.5, 220.9) * mm, "end": v(4.03, 212.96) * mm});
            skArc(sketch, "E27.0.18.3", {"start": v(-4.61, 211.68) * mm, "mid": v(0, 200.6) * mm, "end": v(4.61, 211.68) * mm});
            skArc(sketch, "E27.0.18.4", {"start": v(-4.61, 211.68) * mm, "mid": v(-4.2, 212.27) * mm, "end": v(-4.03, 212.96) * mm});
            skArc(sketch, "E27.0.18.5", {"start": v(4.03, 212.96) * mm, "mid": v(4.2, 212.27) * mm, "end": v(4.61, 211.68) * mm});
            skArc(sketch, "E27.0.19.0", {"start": v(3.5, 182.9) * mm, "mid": v(0, 186.4) * mm, "end": v(-3.5, 182.9) * mm});
            skLineSegment(sketch, "E27.0.19.1", {"start": v(-3.5, 182.9) * mm, "end": v(-4.03, 174.96) * mm});
            skLineSegment(sketch, "E27.0.19.2", {"start": v(3.5, 182.9) * mm, "end": v(4.03, 174.96) * mm});
            skArc(sketch, "E27.0.19.3", {"start": v(-4.61, 173.68) * mm, "mid": v(0, 162.6) * mm, "end": v(4.61, 173.68) * mm});
            skArc(sketch, "E27.0.19.4", {"start": v(-4.61, 173.68) * mm, "mid": v(-4.2, 174.27) * mm, "end": v(-4.03, 174.96) * mm});
            skArc(sketch, "E27.0.19.5", {"start": v(4.03, 174.96) * mm, "mid": v(4.2, 174.27) * mm, "end": v(4.61, 173.68) * mm});
            skArc(sketch, "E27.0.20.0", {"start": v(3.5, 144.9) * mm, "mid": v(0, 148.4) * mm, "end": v(-3.5, 144.9) * mm});
            skLineSegment(sketch, "E27.0.20.1", {"start": v(-3.5, 144.9) * mm, "end": v(-4.03, 136.96) * mm});
            skLineSegment(sketch, "E27.0.20.2", {"start": v(3.5, 144.9) * mm, "end": v(4.03, 136.96) * mm});
            skArc(sketch, "E27.0.20.3", {"start": v(-4.61, 135.68) * mm, "mid": v(0, 124.6) * mm, "end": v(4.61, 135.68) * mm});
            skArc(sketch, "E27.0.20.4", {"start": v(-4.61, 135.68) * mm, "mid": v(-4.2, 136.27) * mm, "end": v(-4.03, 136.96) * mm});
            skArc(sketch, "E27.0.20.5", {"start": v(4.03, 136.96) * mm, "mid": v(4.2, 136.27) * mm, "end": v(4.61, 135.68) * mm});
            skArc(sketch, "E27.0.21.0", {"start": v(3.5, 106.9) * mm, "mid": v(0, 110.4) * mm, "end": v(-3.5, 106.9) * mm});
            skLineSegment(sketch, "E27.0.21.1", {"start": v(-3.5, 106.9) * mm, "end": v(-4.03, 98.96) * mm});
            skLineSegment(sketch, "E27.0.21.2", {"start": v(3.5, 106.9) * mm, "end": v(4.03, 98.96) * mm});
            skArc(sketch, "E27.0.21.3", {"start": v(-4.61, 97.68) * mm, "mid": v(0, 86.6) * mm, "end": v(4.61, 97.68) * mm});
            skArc(sketch, "E27.0.21.4", {"start": v(-4.61, 97.68) * mm, "mid": v(-4.2, 98.27) * mm, "end": v(-4.03, 98.96) * mm});
            skArc(sketch, "E27.0.21.5", {"start": v(4.03, 98.96) * mm, "mid": v(4.2, 98.27) * mm, "end": v(4.61, 97.68) * mm});
            skArc(sketch, "E27.0.22.0", {"start": v(3.5, 68.9) * mm, "mid": v(0, 72.4) * mm, "end": v(-3.5, 68.9) * mm});
            skLineSegment(sketch, "E27.0.22.1", {"start": v(-3.5, 68.9) * mm, "end": v(-4.03, 60.96) * mm});
            skLineSegment(sketch, "E27.0.22.2", {"start": v(3.5, 68.9) * mm, "end": v(4.03, 60.96) * mm});
            skArc(sketch, "E27.0.22.3", {"start": v(-4.61, 59.68) * mm, "mid": v(0, 48.6) * mm, "end": v(4.61, 59.68) * mm});
            skArc(sketch, "E27.0.22.4", {"start": v(-4.61, 59.68) * mm, "mid": v(-4.2, 60.27) * mm, "end": v(-4.03, 60.96) * mm});
            skArc(sketch, "E27.0.22.5", {"start": v(4.03, 60.96) * mm, "mid": v(4.2, 60.27) * mm, "end": v(4.61, 59.68) * mm});
            skArc(sketch, "E27.0.23.0", {"start": v(3.5, 30.9) * mm, "mid": v(0, 34.4) * mm, "end": v(-3.5, 30.9) * mm});
            skLineSegment(sketch, "E27.0.23.1", {"start": v(-3.5, 30.9) * mm, "end": v(-4.03, 22.96) * mm});
            skLineSegment(sketch, "E27.0.23.2", {"start": v(3.5, 30.9) * mm, "end": v(4.03, 22.96) * mm});
            skArc(sketch, "E27.0.23.3", {"start": v(-4.61, 21.68) * mm, "mid": v(0, 10.6) * mm, "end": v(4.61, 21.68) * mm});
            skArc(sketch, "E27.0.23.4", {"start": v(-4.61, 21.68) * mm, "mid": v(-4.2, 22.27) * mm, "end": v(-4.03, 22.96) * mm});
            skArc(sketch, "E27.0.23.5", {"start": v(4.03, 22.96) * mm, "mid": v(4.2, 22.27) * mm, "end": v(4.61, 21.68) * mm});
            skLineSegment(sketch, "E27.direction1", {"start": v(-3.5, 904.9) * mm, "end": v(21.5, 904.9) * mm, "construction": true});
            skLineSegment(sketch, "E27.direction2", {"start": v(-3.5, 904.9) * mm, "end": v(-3.5, 866.9) * mm, "construction": true});
            skSolve(sketch);
        }
        {
            var Q0;
            Q0=makeQuery(id+"F4.imprint","IMPRINT",FACE,{"disambiguationData":[TD([[makeQuery(id+"F4.imprint","IMPRINT",EDGE,{"derivedFrom":sQuery(id+"F4.wireOp",EDGE,"E18")}),1.0]])]});
            var Q1;
            Q1=makeQuery(id+"F4.imprint","IMPRINT",FACE,{"disambiguationData":[TD([[makeQuery(id+"F4.imprint","IMPRINT",EDGE,{"derivedFrom":sQuery(id+"F4.wireOp",EDGE,"E27.0.1.0")}),1.0]])]});
            var Q2;
            Q2=makeQuery(id+"F4.imprint","IMPRINT",FACE,{"disambiguationData":[TD([[makeQuery(id+"F4.imprint","IMPRINT",EDGE,{"derivedFrom":sQuery(id+"F4.wireOp",EDGE,"E27.0.2.0")}),1.0]])]});
            var Q3;
            Q3=makeQuery(id+"F4.imprint","IMPRINT",FACE,{"disambiguationData":[TD([[makeQuery(id+"F4.imprint","IMPRINT",EDGE,{"derivedFrom":sQuery(id+"F4.wireOp",EDGE,"E27.0.3.0")}),1.0]])]});
            var Q4;
            Q4=makeQuery(id+"F4.imprint","IMPRINT",FACE,{"disambiguationData":[TD([[makeQuery(id+"F4.imprint","IMPRINT",EDGE,{"derivedFrom":sQuery(id+"F4.wireOp",EDGE,"E27.0.4.0")}),1.0]])]});
            var Q5;
            Q5=makeQuery(id+"F4.imprint","IMPRINT",FACE,{"disambiguationData":[TD([[makeQuery(id+"F4.imprint","IMPRINT",EDGE,{"derivedFrom":sQuery(id+"F4.wireOp",EDGE,"E27.0.5.0")}),1.0]])]});
            var Q6;
            Q6=makeQuery(id+"F4.imprint","IMPRINT",FACE,{"disambiguationData":[TD([[makeQuery(id+"F4.imprint","IMPRINT",EDGE,{"derivedFrom":sQuery(id+"F4.wireOp",EDGE,"E27.0.6.0")}),1.0]])]});
            var Q7;
            Q7=makeQuery(id+"F4.imprint","IMPRINT",FACE,{"disambiguationData":[TD([[makeQuery(id+"F4.imprint","IMPRINT",EDGE,{"derivedFrom":sQuery(id+"F4.wireOp",EDGE,"E27.0.7.0")}),1.0]])]});
            var Q8;
            Q8=makeQuery(id+"F4.imprint","IMPRINT",FACE,{"disambiguationData":[TD([[makeQuery(id+"F4.imprint","IMPRINT",EDGE,{"derivedFrom":sQuery(id+"F4.wireOp",EDGE,"E27.0.8.0")}),1.0]])]});
            var Q9;
            Q9=makeQuery(id+"F4.imprint","IMPRINT",FACE,{"disambiguationData":[TD([[makeQuery(id+"F4.imprint","IMPRINT",EDGE,{"derivedFrom":sQuery(id+"F4.wireOp",EDGE,"E27.0.9.0")}),1.0]])]});
            var Q10;
            Q10=makeQuery(id+"F4.imprint","IMPRINT",FACE,{"disambiguationData":[TD([[makeQuery(id+"F4.imprint","IMPRINT",EDGE,{"derivedFrom":sQuery(id+"F4.wireOp",EDGE,"E27.0.10.0")}),1.0]])]});
            var Q11;
            Q11=makeQuery(id+"F4.imprint","IMPRINT",FACE,{"disambiguationData":[TD([[makeQuery(id+"F4.imprint","IMPRINT",EDGE,{"derivedFrom":sQuery(id+"F4.wireOp",EDGE,"E27.0.11.0")}),1.0]])]});
            var Q12;
            Q12=makeQuery(id+"F4.imprint","IMPRINT",FACE,{"disambiguationData":[TD([[makeQuery(id+"F4.imprint","IMPRINT",EDGE,{"derivedFrom":sQuery(id+"F4.wireOp",EDGE,"E27.0.12.0")}),1.0]])]});
            var Q13;
            Q13=makeQuery(id+"F4.imprint","IMPRINT",FACE,{"disambiguationData":[TD([[makeQuery(id+"F4.imprint","IMPRINT",EDGE,{"derivedFrom":sQuery(id+"F4.wireOp",EDGE,"E27.0.13.0")}),1.0]])]});
            var Q14;
            Q14=makeQuery(id+"F4.imprint","IMPRINT",FACE,{"disambiguationData":[TD([[makeQuery(id+"F4.imprint","IMPRINT",EDGE,{"derivedFrom":sQuery(id+"F4.wireOp",EDGE,"E27.0.14.0")}),1.0]])]});
            var Q15;
            Q15=makeQuery(id+"F4.imprint","IMPRINT",FACE,{"disambiguationData":[TD([[makeQuery(id+"F4.imprint","IMPRINT",EDGE,{"derivedFrom":sQuery(id+"F4.wireOp",EDGE,"E27.0.15.0")}),1.0]])]});
            var Q16;
            Q16=makeQuery(id+"F4.imprint","IMPRINT",FACE,{"disambiguationData":[TD([[makeQuery(id+"F4.imprint","IMPRINT",EDGE,{"derivedFrom":sQuery(id+"F4.wireOp",EDGE,"E27.0.16.0")}),1.0]])]});
            var Q17;
            Q17=makeQuery(id+"F4.imprint","IMPRINT",FACE,{"disambiguationData":[TD([[makeQuery(id+"F4.imprint","IMPRINT",EDGE,{"derivedFrom":sQuery(id+"F4.wireOp",EDGE,"E27.0.17.0")}),1.0]])]});
            var Q18;
            Q18=makeQuery(id+"F4.imprint","IMPRINT",FACE,{"disambiguationData":[TD([[makeQuery(id+"F4.imprint","IMPRINT",EDGE,{"derivedFrom":sQuery(id+"F4.wireOp",EDGE,"E27.0.18.0")}),1.0]])]});
            var Q19;
            Q19=makeQuery(id+"F4.imprint","IMPRINT",FACE,{"disambiguationData":[TD([[makeQuery(id+"F4.imprint","IMPRINT",EDGE,{"derivedFrom":sQuery(id+"F4.wireOp",EDGE,"E27.0.19.0")}),1.0]])]});
            var Q20;
            Q20=makeQuery(id+"F4.imprint","IMPRINT",FACE,{"disambiguationData":[TD([[makeQuery(id+"F4.imprint","IMPRINT",EDGE,{"derivedFrom":sQuery(id+"F4.wireOp",EDGE,"E27.0.20.0")}),1.0]])]});
            var Q21;
            Q21=makeQuery(id+"F4.imprint","IMPRINT",FACE,{"disambiguationData":[TD([[makeQuery(id+"F4.imprint","IMPRINT",EDGE,{"derivedFrom":sQuery(id+"F4.wireOp",EDGE,"E27.0.21.0")}),1.0]])]});
            var Q22;
            Q22=makeQuery(id+"F4.imprint","IMPRINT",FACE,{"disambiguationData":[TD([[makeQuery(id+"F4.imprint","IMPRINT",EDGE,{"derivedFrom":sQuery(id+"F4.wireOp",EDGE,"E27.0.22.0")}),1.0]])]});
            var Q23;
            Q23=makeQuery(id+"F4.imprint","IMPRINT",FACE,{"disambiguationData":[TD([[makeQuery(id+"F4.imprint","IMPRINT",EDGE,{"derivedFrom":sQuery(id+"F4.wireOp",EDGE,"E27.0.23.0")}),1.0]])]});
            extrude(context, id + "F5", {"entities" : qUnion([Q0, Q1, Q2, Q3, Q4, Q5, Q6, Q7, Q8, Q9, Q10, Q11, Q12, Q13, Q14, Q15, Q16, Q17, Q18, Q19, Q20, Q21, Q22, Q23]), "operationType" : NewBodyOperationType.REMOVE, "endBound" : BoundingType.UP_TO_NEXT, "oppositeDirection" : true, "depth" : 25 * mm});
        }
        {
            var Q0;
            Q0=makeQuery(id+"F1.opExtrude","SWEPT_FACE",FACE,{"disambiguationData":[OSD([sQuery(id+"F0.wireOp",EDGE,"E1.0"),sQuery(id+"F0.wireOp",EDGE,"E2")])]});
            var sketch = newSketch(context, id + "F6", { "sketchPlane" : qUnion([Q0])});
            skArc(sketch, "E28.0", {"start": v(4.61, 667.68) * mm, "mid": v(0, 656.6) * mm, "end": v(-4.61, 667.68) * mm});
            skArc(sketch, "E28.1", {"start": v(4.61, 705.68) * mm, "mid": v(0, 694.6) * mm, "end": v(-4.61, 705.68) * mm});
            skLineSegment(sketch, "E28.2", {"start": v(-12.9, 710.1) * mm, "end": v(-12.9, 643.2) * mm});
            skArc(sketch, "E29", {"start": v(4.61, 667.68) * mm, "mid": v(0, 669.6) * mm, "end": v(-4.61, 667.68) * mm});
            skArc(sketch, "E30", {"start": v(4.61, 705.68) * mm, "mid": v(0, 707.6) * mm, "end": v(-4.61, 705.68) * mm});
            skLineSegment(sketch, "E31.bottom", {"start": v(-12.9, 710.1) * mm, "end": v(592.1, 710.1) * mm});
            skLineSegment(sketch, "E31.top", {"start": v(-12.9, 643.2) * mm, "end": v(592.1, 643.2) * mm});
            skLineSegment(sketch, "E31.right", {"start": v(592.1, 710.1) * mm, "end": v(592.1, 643.2) * mm});
            skPoint(sketch, "E32.orphan", {"position": v(-12.9, 0) * mm});
            skPoint(sketch, "E33.orphan", {"position": v(-12.9, 914.4) * mm});
            skSolve(sketch);
        }
        {
            var Q0;
            {var subQ0=sQuery(id+"F6.wireOp",EDGE,"E31.right");Q0=makeQuery(id+"F6.imprint","IMPRINT",FACE,{"disambiguationData":[TD([[makeQuery(id+"F6.imprint","IMPRINT",EDGE,{"derivedFrom":subQ0}),-1.0]])]});}
            var Q1;
            Q1=makeQuery(id+"F6.imprint","IMPRINT",FACE,{"disambiguationData":[TD([[makeQuery(id+"F6.imprint","IMPRINT",EDGE,{"derivedFrom":sQuery(id+"F6.wireOp",EDGE,"E28.0")}),1.0]])]});
            var Q2;
            Q2=makeQuery(id+"F6.imprint","IMPRINT",FACE,{"disambiguationData":[TD([[makeQuery(id+"F6.imprint","IMPRINT",EDGE,{"derivedFrom":sQuery(id+"F6.wireOp",EDGE,"E28.0")}),-1.0]])]});
            var Q3;
            Q3=makeQuery(id+"F6.imprint","IMPRINT",FACE,{"disambiguationData":[TD([[makeQuery(id+"F6.imprint","IMPRINT",EDGE,{"derivedFrom":sQuery(id+"F6.wireOp",EDGE,"E28.1")}),-1.0]])]});
            var Q4;
            Q4=makeQuery(id+"F6.imprint","IMPRINT",FACE,{"disambiguationData":[TD([[makeQuery(id+"F6.imprint","IMPRINT",EDGE,{"derivedFrom":sQuery(id+"F6.wireOp",EDGE,"E29")}),-1.0]])]});
            var Q5;
            Q5=makeQuery(id+"F6.imprint","IMPRINT",FACE,{"disambiguationData":[TD([[makeQuery(id+"F6.imprint","IMPRINT",EDGE,{"derivedFrom":sQuery(id+"F6.wireOp",EDGE,"E30")}),-1.0]])]});
            extrude(context, id + "F7", {"entities" : qUnion([Q0, Q1, Q2, Q3, Q4, Q5]), "depth" : 2 * mm});
        }
        {
            var Q0;
            Q0=makeQuery(id+"F7.opExtrude","CAP_FACE",FACE,{"disambiguationData":[OSD([sQuery(id+"F6.wireOp",EDGE,"E31.bottom"),sQuery(id+"F6.wireOp",EDGE,"E31.top"),sQuery(id+"F6.wireOp",EDGE,"E28.2"),sQuery(id+"F6.wireOp",EDGE,"E31.right")])],"isStart":true});
            var sketch = newSketch(context, id + "F8", { "sketchPlane" : qUnion([Q0])});
            skArc(sketch, "E34.0", {"start": v(-4.61, 667.68) * mm, "mid": v(0, 656.6) * mm, "end": v(4.61, 667.68) * mm, "construction": true});
            skArc(sketch, "E35.0", {"start": v(-4.61, 705.68) * mm, "mid": v(0, 694.6) * mm, "end": v(4.61, 705.68) * mm, "construction": true});
            skCircle(sketch, "E36", {"center": v(0, 663.1) * mm, "radius": 3.25 * mm});
            skCircle(sketch, "E37", {"center": v(0, 701.1) * mm, "radius": 3.25 * mm});
            skSolve(sketch);
        }
        {
            var Q0;
            Q0 = qSketchRegion(id + "F8", true);
            extrude(context, id + "F9", {"entities" : qUnion([Q0]), "operationType" : NewBodyOperationType.ADD, "depth" : 2 * mm});
        }
        {
            var Q0;
            Q0=makeQuery(id+"F9.opExtrude","CAP_FACE",FACE,{"disambiguationData":[OSD([sQuery(id+"F8.wireOp",EDGE,"E36")])],"isStart":false});
            var sketch = newSketch(context, id + "F10", { "sketchPlane" : qUnion([Q0])});
            skCircle(sketch, "E38", {"center": v(0, 663.1) * mm, "radius": 6.25 * mm});
            skSolve(sketch);
        }
        {
            var Q0;
            Q0 = qSketchRegion(id + "F10", true);
            extrude(context, id + "F11", {"entities" : qUnion([Q0]), "operationType" : NewBodyOperationType.ADD, "depth" : 2 * mm});
        }
        {
            var Q0;
            Q0=makeQuery(id+"F11.opExtrude","CAP_FACE",FACE,{"disambiguationData":[OSD([sQuery(id+"F10.wireOp",EDGE,"E38")])],"isStart":false});
            fillet(context, id + "F12", {"entities" : qUnion([Q0]), "radius" : .5 * mm, "tangentPropagation" : true, "allowEdgeOverflow" : false});
        }
        {
            var Q0;
            Q0=makeQuery(id+"F9.opExtrude","CAP_FACE",FACE,{"disambiguationData":[OSD([sQuery(id+"F8.wireOp",EDGE,"E37")])],"isStart":false});
            var sketch = newSketch(context, id + "F13", { "sketchPlane" : qUnion([Q0])});
            skCircle(sketch, "E39", {"center": v(0, 701.1) * mm, "radius": 6.25 * mm});
            skSolve(sketch);
        }
        {
            var Q0;
            Q0 = qSketchRegion(id + "F13", true);
            extrude(context, id + "F14", {"entities" : qUnion([Q0]), "operationType" : NewBodyOperationType.ADD, "depth" : 2 * mm});
        }
        {
            var Q0;
            Q0=makeQuery(id+"F14.opExtrude","CAP_FACE",FACE,{"disambiguationData":[OSD([sQuery(id+"F13.wireOp",EDGE,"E39")])],"isStart":false});
            fillet(context, id + "F15", {"entities" : qUnion([Q0]), "radius" : .5 * mm, "tangentPropagation" : true, "allowEdgeOverflow" : false});
        }
        {
            var Q0;
            Q0=makeQuery(id+"F7.opExtrude","SWEPT_BODY",BODY,{"disambiguationData":[OSD([sQuery(id+"F6.wireOp",EDGE,"E31.bottom"),sQuery(id+"F6.wireOp",EDGE,"E31.top"),sQuery(id+"F6.wireOp",EDGE,"E28.2"),sQuery(id+"F6.wireOp",EDGE,"E31.right")])]});
            var Q1;
            Q1=makeQuery(id+"F7.opExtrude","SWEPT_FACE",FACE,{"disambiguationData":[OSD([sQuery(id+"F6.wireOp",EDGE,"E31.right")])]});
            mirror(context, id + "F16", {"operationType" : NewBodyOperationType.ADD, "entities" : qUnion([Q0]), "mirrorPlane" : qUnion([Q1])});
        }
        {
            var Q0;
            Q0=makeQuery(id+"F7.opExtrude","SWEPT_FACE",FACE,{"disambiguationData":[OSD([sQuery(id+"F6.wireOp",EDGE,"E28.2")])]});
            var sketch = newSketch(context, id + "F17", { "sketchPlane" : qUnion([Q0])});
            skLineSegment(sketch, "E40", {"start": v(-11.9, 643.2) * mm, "end": v(5.7, 643.2) * mm});
            skLineSegment(sketch, "E41", {"start": v(5.7, 643.2) * mm, "end": v(5.7, 645.2) * mm});
            skLineSegment(sketch, "E42", {"start": v(5.7, 645.2) * mm, "end": v(-11.9, 645.2) * mm});
            skLineSegment(sketch, "E43", {"start": v(-11.9, 645.2) * mm, "end": v(-11.9, 643.2) * mm});
            skSolve(sketch);
        }
        {
            var Q0;
            Q0 = qSketchRegion(id + "F17", true);
            extrude(context, id + "F18", {"entities" : qUnion([Q0]), "operationType" : NewBodyOperationType.ADD, "oppositeDirection" : true, "depth" : 1210 * mm});
        }
        {
            var Q0;
            {var subQ0=makeQuery(id+"F7.opExtrude","CAP_EDGE",EDGE,{"disambiguationData":[OSD([sQuery(id+"F6.wireOp",EDGE,"E31.top")])],"isStart":true});Q0=makeQuery(id+"F16.boolean.opBoolean","MERGE",EDGE,{"derivedFrom":[subQ0,makeQuery(id+"F16.opPattern","COPY",EDGE,{"derivedFrom":subQ0,"instanceName":"1"})]});}
            var Q1;
            Q1=makeQuery(id+"F18.opExtrude","SWEPT_EDGE",EDGE,{"disambiguationData":[OSD([sQuery(id+"F6.wireOp",EDGE,"E28.2"),sQuery(id+"F17.wireOp",EDGE,"E42"),sQuery(id+"F17.wireOp",EDGE,"E43")])]});
            fillet(context, id + "F19", {"entities" : qUnion([Q0, Q1]), "radius" : .5 * mm, "tangentPropagation" : true, "allowEdgeOverflow" : false});
        }
    });
